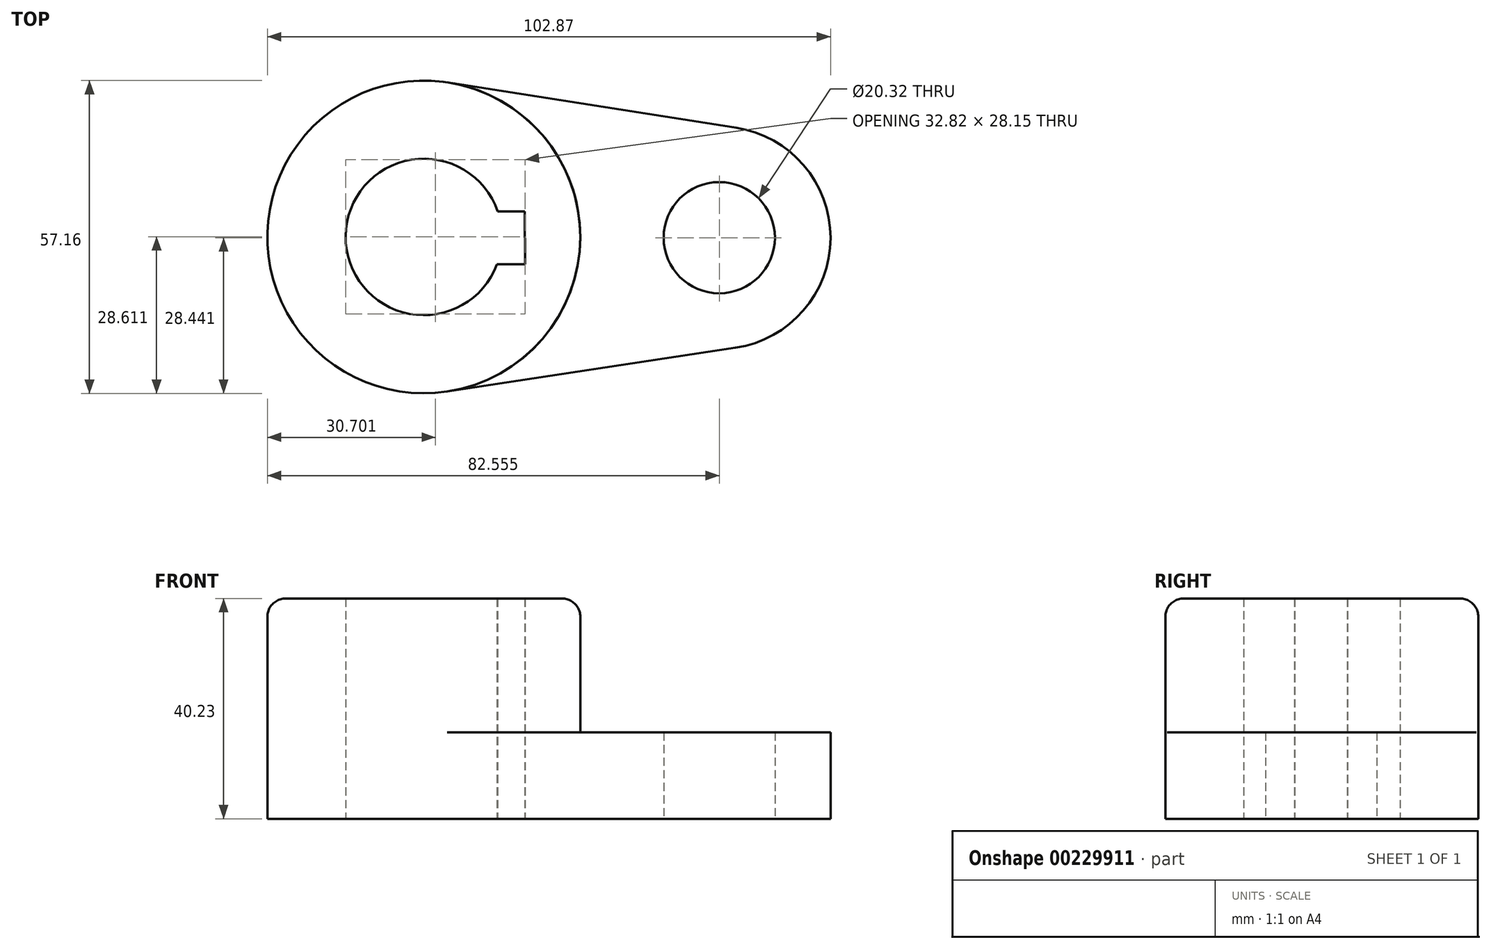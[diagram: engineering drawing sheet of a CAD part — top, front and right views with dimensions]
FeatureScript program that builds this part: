
annotation { "Feature Type Name" : "Feature", "Feature Type Description" : "" }
export const myFeature = defineFeature(function(context is Context, id is Id, definition is map)
    precondition{}
    {
        {
            var Q0;
            Q0=qCreatedBy(makeId("Top.planeOp"),FACE);
            var sketch = newSketch(context, id + "F0", { "sketchPlane" : qUnion([Q0])});
            skCircle(sketch, "E0", {"center": v(0, 0) * mm, "radius": 28.58 * mm});
            skArc(sketch, "E1", {"start": v(13.5, 4.66) * mm, "mid": v(-14.29, 0.18) * mm, "end": v(13.39, -5) * mm});
            skLineSegment(sketch, "E2", {"start": v(18.47, 4.69) * mm, "end": v(18.53, -4.96) * mm});
            skLineSegment(sketch, "E3", {"start": v(18.47, 4.69) * mm, "end": v(13.5, 4.66) * mm});
            skLineSegment(sketch, "E4", {"start": v(18.53, -4.96) * mm, "end": v(13.39, -5) * mm});
            skLineSegment(sketch, "E5", {"start": v(0, 0) * mm, "end": v(53.97, -0.14) * mm});
            skPoint(sketch, "E5.endSnap0", {"position": v(18.5, -0.14) * mm});
            skCircle(sketch, "E6", {"center": v(53.97, -0.14) * mm, "radius": 10.16 * mm});
            skArc(sketch, "E7", {"start": v(56.92, -20.24) * mm, "mid": v(74.3, -0.19) * mm, "end": v(57.01, 19.95) * mm});
            skLineSegment(sketch, "E8", {"start": v(57.01, 19.95) * mm, "end": v(4.44, 28.23) * mm});
            skLineSegment(sketch, "E9", {"start": v(56.92, -20.24) * mm, "end": v(4.3, -28.25) * mm});
            skSolve(sketch);
        }
        {
            var Q0;
            Q0=makeQuery(id+"F0.imprint","IMPRINT",FACE,{"disambiguationData":[TD([[makeQuery(id+"F0.imprint","IMPRINT",EDGE,{"derivedFrom":sQuery(id+"F0.wireOp",EDGE,"E1")}),-1.0]])]});
            var Q1;
            Q1=makeQuery(id+"F0.imprint","IMPRINT",FACE,{"disambiguationData":[TD([[makeQuery(id+"F0.imprint","IMPRINT",EDGE,{"derivedFrom":sQuery(id+"F0.wireOp",EDGE,"tA3lKswW-VY7z-UD9m-lsk2-yWj2fZMJU8Nv")}),-1.0]])]});
            var Q2;
            Q2=makeQuery(id+"F0.imprint","IMPRINT",FACE,{"disambiguationData":[TD([[makeQuery(id+"F0.imprint","IMPRINT",EDGE,{"derivedFrom":sQuery(id+"F0.wireOp",EDGE,"E6")}),-1.0]])]});
            extrude(context, id + "F1", {"entities" : qUnion([Q0, Q1, Q2]), "depth" : 15.77 * mm});
        }
        {
            var Q0;
            Q0=makeQuery(id+"F0.imprint","IMPRINT",FACE,{"disambiguationData":[TD([[makeQuery(id+"F0.imprint","IMPRINT",EDGE,{"derivedFrom":sQuery(id+"F0.wireOp",EDGE,"E1")}),-1.0]])]});
            extrude(context, id + "F2", {"entities" : qUnion([Q0]), "operationType" : NewBodyOperationType.ADD, "depth" : 40.23 * mm});
        }
        {
            var Q0;
            Q0=makeQuery(id+"F2.opExtrude","CAP_EDGE",EDGE,{"disambiguationData":[OSD([sQuery(id+"F0.wireOp",EDGE,"E0")])],"isStart":false});
            fillet(context, id + "F3", {"entities" : qUnion([Q0]), "radius" : 3.3 * mm, "tangentPropagation" : true, "allowEdgeOverflow" : false});
        }
    });
